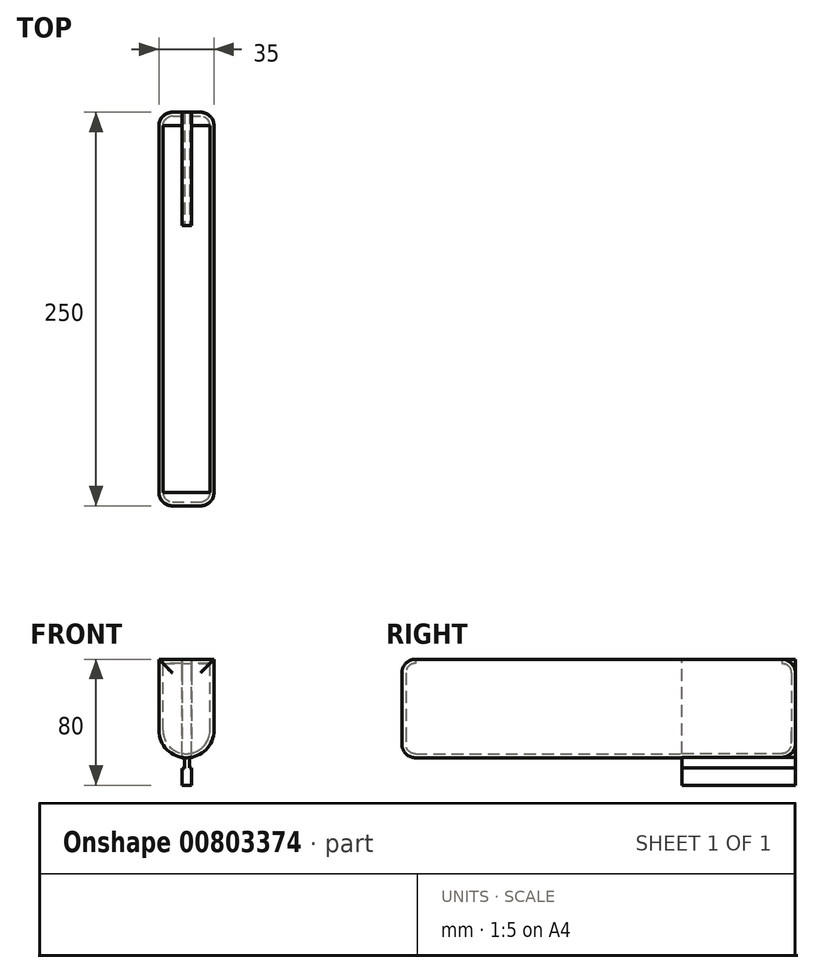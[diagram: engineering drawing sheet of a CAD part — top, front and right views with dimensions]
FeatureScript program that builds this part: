
annotation { "Feature Type Name" : "Feature", "Feature Type Description" : "" }
export const myFeature = defineFeature(function(context is Context, id is Id, definition is map)
    precondition{}
    {
        {
            var Q0;
            Q0=qCreatedBy(makeId("Top.planeOp"),FACE);
            var sketch = newSketch(context, id + "F0", { "sketchPlane" : qUnion([Q0])});
            skLineSegment(sketch, "E0.bottom", {"start": v(0, 0) * mm, "end": v(35, 0) * mm});
            skLineSegment(sketch, "E0.top", {"start": v(0, -250) * mm, "end": v(35, -250) * mm});
            skLineSegment(sketch, "E0.left", {"start": v(0, 0) * mm, "end": v(0, -250) * mm});
            skLineSegment(sketch, "E0.right", {"start": v(35, 0) * mm, "end": v(35, -250) * mm});
            skSolve(sketch);
        }
        {
            var Q0;
            Q0 = qSketchRegion(id + "F0", true);
            var Q1;
            Q1=makeQuery(id+"F0.imprint","IMPRINT",FACE,{"disambiguationData":[TD([[makeQuery(id+"F0.imprint","IMPRINT",EDGE,{"derivedFrom":sQuery(id+"F0.wireOp",EDGE,"E0.bottom")}),-1.0]])]});
            extrude(context, id + "F1", {"entities" : qUnion([Q0, Q1]), "oppositeDirection" : true, "depth" : 80 * mm - 35 * mm, "offsetDistance" : 25.4 * mm});
        }
        {
            var Q0;
            Q0=makeQuery(id+"F1.opExtrude","SWEPT_FACE",FACE,{"disambiguationData":[OSD([sQuery(id+"F0.wireOp",EDGE,"E0.bottom")])]});
            var sketch = newSketch(context, id + "F2", { "sketchPlane" : qUnion([Q0])});
            skCircle(sketch, "E1", {"center": v(-17.5, -45) * mm, "radius": 17.5 * mm});
            skLineSegment(sketch, "E2", {"start": v(-17.5, -45) * mm, "end": v(-35, -45) * mm});
            skLineSegment(sketch, "E3", {"start": v(-35, -45) * mm, "end": v(-17.5, -45) * mm});
            skLineSegment(sketch, "E4", {"start": v(0, -45) * mm, "end": v(-17.5, -45) * mm});
            skLineSegment(sketch, "E5", {"start": v(0, -45) * mm, "end": v(0, -27.5) * mm});
            skLineSegment(sketch, "E6", {"start": v(0, -27.5) * mm, "end": v(-17.5, -27.5) * mm});
            skLineSegment(sketch, "E7", {"start": v(-35, -27.5) * mm, "end": v(-17.5, -27.5) * mm});
            skSolve(sketch);
        }
        {
            var Q0;
            Q0 = qSketchRegion(id + "F2", true);
            var Q1;
            Q1=makeQuery(id+"F2.imprint","IMPRINT",FACE,{"disambiguationData":[TD([[makeQuery(id+"F2.imprint","IMPRINT",EDGE,{"derivedFrom":sQuery(id+"F2.wireOp",EDGE,"ydjFsPhl-Mdwv-BTvX-MJDi-FNe1oPPKUGmP")}),1.0]])]});
            extrude(context, id + "F3", {"entities" : qUnion([Q0, Q1]), "operationType" : NewBodyOperationType.ADD, "oppositeDirection" : true, "depth" : 250 * mm, "offsetDistance" : 25.4 * mm});
        }
        {
            var Q0;
            Q0 = qSketchRegion(id + "F2", true);
            var Q1;
            Q1=makeQuery(id+"F2.imprint","IMPRINT",FACE,{"disambiguationData":[TD([[makeQuery(id+"F2.imprint","IMPRINT",EDGE,{"derivedFrom":sQuery(id+"F2.wireOp",EDGE,"AiNuS2eF-7K4i-NF9d-Ntjd-DSRlubpccXRD")}),1.0]])]});
            extrude(context, id + "F4", {"entities" : qUnion([Q0, Q1]), "operationType" : NewBodyOperationType.ADD, "oppositeDirection" : true, "depth" : 250 * mm, "offsetDistance" : 25.4 * mm});
        }
        {
            var Q0;
            Q0=makeQuery(id+"F3.boolean.opBoolean","MERGE",FACE,{"derivedFrom":[makeQuery(id+"F1.opExtrude","SWEPT_FACE",FACE,{"disambiguationData":[OSD([sQuery(id+"F0.wireOp",EDGE,"E0.bottom")])]}),makeQuery(id+"F3.opExtrude","CAP_FACE",FACE,{"disambiguationData":[OSD([sQuery(id+"F2.wireOp",EDGE,"E1"),sQuery(id+"F2.wireOp",EDGE,"E5"),sQuery(id+"F2.wireOp",EDGE,"E6")])],"isStart":true})]});
            var Q1;
            Q1=makeQuery(id+"F3.boolean.opBoolean","MERGE",FACE,{"derivedFrom":[makeQuery(id+"F1.opExtrude","SWEPT_FACE",FACE,{"disambiguationData":[OSD([sQuery(id+"F0.wireOp",EDGE,"E0.top")])]}),makeQuery(id+"F3.opExtrude","CAP_FACE",FACE,{"disambiguationData":[OSD([sQuery(id+"F2.wireOp",EDGE,"E1"),sQuery(id+"F2.wireOp",EDGE,"E5"),sQuery(id+"F2.wireOp",EDGE,"E6")])],"isStart":false})]});
            fillet(context, id + "F5", {"entities" : qUnion([Q0, Q1]), "radius" : 8.58 * mm, "tangentPropagation" : true, "allowEdgeOverflow" : false});
        }
        {
            var Q0;
            Q0=makeQuery(id+"F1.opExtrude","CAP_FACE",FACE,{"disambiguationData":[OSD([sQuery(id+"F0.wireOp",EDGE,"E0.bottom"),sQuery(id+"F0.wireOp",EDGE,"E0.top"),sQuery(id+"F0.wireOp",EDGE,"E0.left"),sQuery(id+"F0.wireOp",EDGE,"E0.right")])],"isStart":true});
            shell(context, id + "F6", {"entities" : qUnion([Q0]), "thickness" : 2.54 * mm});
        }
        {
            var Q0;
            Q0=qCreatedBy(makeId("Top.planeOp"),FACE);
            var sketch = newSketch(context, id + "F7", { "sketchPlane" : qUnion([Q0])});
            skLineSegment(sketch, "E8.bottom", {"start": v(14.64, 0) * mm, "end": v(20.84, 0) * mm});
            skLineSegment(sketch, "E8.top", {"start": v(14.64, -72.05) * mm, "end": v(20.84, -72.05) * mm});
            skLineSegment(sketch, "E8.left", {"start": v(14.64, 0) * mm, "end": v(14.64, -72.05) * mm});
            skLineSegment(sketch, "E8.right", {"start": v(20.84, 0) * mm, "end": v(20.84, -72.05) * mm});
            skLineSegment(sketch, "E9", {"start": v(20.84, 0) * mm, "end": v(14.64, 0) * mm});
            skSolve(sketch);
        }
        {
            var Q0;
            Q0 = qSketchRegion(id + "F7", true);
            extrude(context, id + "F8", {"entities" : qUnion([Q0]), "operationType" : NewBodyOperationType.ADD, "oppositeDirection" : true, "depth" : 80 * mm, "offsetDistance" : 25.4 * mm});
        }
        {
            var Q0;
            {var subQ2=sQuery(id+"F7.wireOp",EDGE,"E8.top");Q0=makeQuery(id+"F8.boolean.opBoolean","SPLIT",FACE,{"disambiguationData":[TD([makeQuery(id+"F3.opExtrude","SWEPT_FACE",FACE,{"disambiguationData":[OSD([sQuery(id+"F2.wireOp",EDGE,"E1")])]})])],"derivedFrom":makeQuery(id+"F8.opExtrude","SWEPT_FACE",FACE,{"disambiguationData":[OSD([subQ2])]})});}
            var sketch = newSketch(context, id + "F9", { "sketchPlane" : qUnion([Q0])});
            skLineSegment(sketch, "E10", {"start": v(16.46, -62.47) * mm, "end": v(16.46, -69.2) * mm});
            skLineSegment(sketch, "E11", {"start": v(16.46, -69.2) * mm, "end": v(14.64, -69.2) * mm});
            skLineSegment(sketch, "E12", {"start": v(14.64, -69.2) * mm, "end": v(14.64, -62.54) * mm});
            skLineSegment(sketch, "E13", {"start": v(14.64, -62.54) * mm, "end": v(16.46, -62.47) * mm});
            skLineSegment(sketch, "E14", {"start": v(19.57, -62.38) * mm, "end": v(19.57, -69.1) * mm});
            skLineSegment(sketch, "E15", {"start": v(19.57, -69.1) * mm, "end": v(20.84, -69.1) * mm});
            skLineSegment(sketch, "E16", {"start": v(20.84, -69.1) * mm, "end": v(20.84, -62.18) * mm});
            skLineSegment(sketch, "E17", {"start": v(20.84, -62.18) * mm, "end": v(19.57, -62.38) * mm});
            skSolve(sketch);
        }
        {
            var Q0;
            Q0 = qSketchRegion(id + "F9", true);
            extrude(context, id + "F10", {"entities" : qUnion([Q0]), "operationType" : NewBodyOperationType.REMOVE, "oppositeDirection" : true, "depth" : 101.35 * mm, "offsetDistance" : 25.4 * mm});
        }
    });
